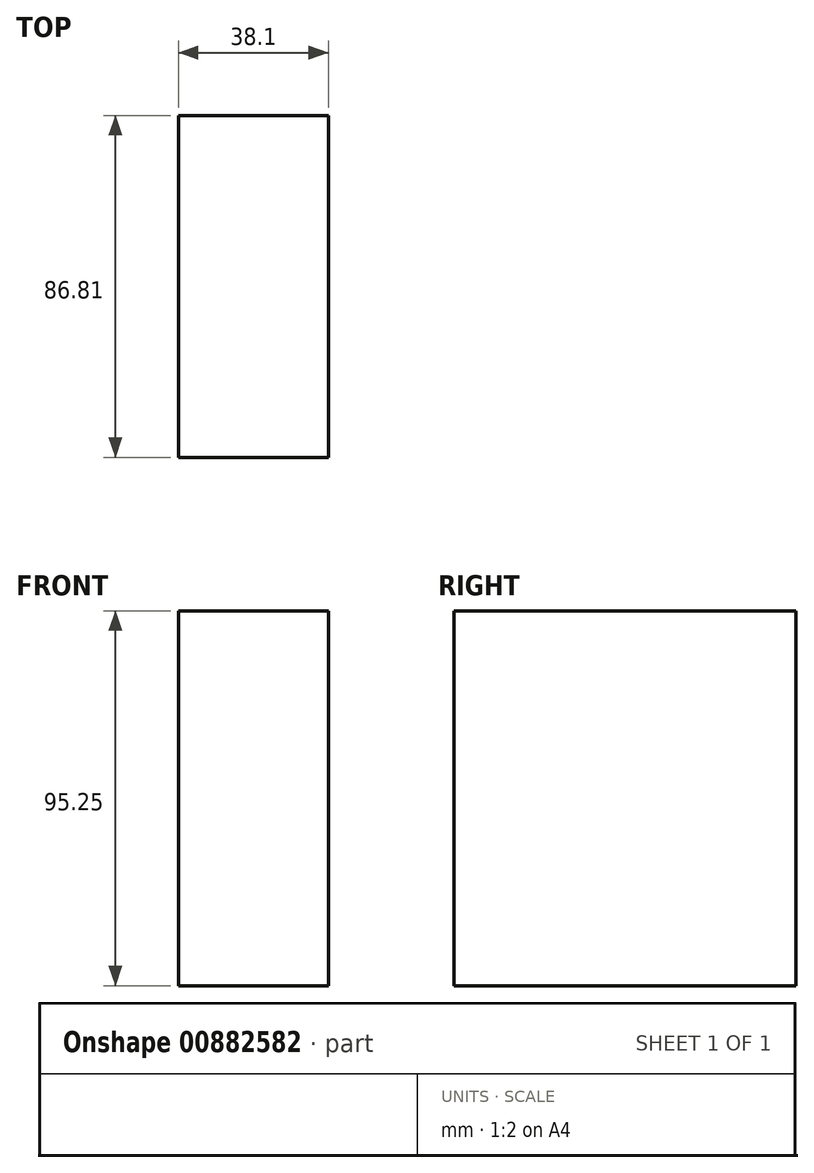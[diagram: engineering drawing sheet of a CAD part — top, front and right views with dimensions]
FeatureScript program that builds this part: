
annotation { "Feature Type Name" : "Feature", "Feature Type Description" : "" }
export const myFeature = defineFeature(function(context is Context, id is Id, definition is map)
    precondition{}
    {
        {
            var Q0;
            Q0=qCreatedBy(makeId("Front.planeOp"),FACE);
            var sketch = newSketch(context, id + "F0", { "sketchPlane" : qUnion([Q0])});
            skLineSegment(sketch, "E0.bottom", {"start": v(0, 0) * mm, "end": v(76.2, 0) * mm});
            skLineSegment(sketch, "E0.top", {"start": v(0, 95.25) * mm, "end": v(76.2, 95.25) * mm});
            skLineSegment(sketch, "E0.left", {"start": v(0, 0) * mm, "end": v(0, 95.25) * mm});
            skLineSegment(sketch, "E0.right", {"start": v(76.2, 0) * mm, "end": v(76.2, 95.25) * mm});
            skSolve(sketch);
        }
        {
            var Q0;
            Q0=makeQuery(id+"F0.imprint","IMPRINT",FACE,{"disambiguationData":[TD([[makeQuery(id+"F0.imprint","IMPRINT",EDGE,{"derivedFrom":sQuery(id+"F0.wireOp",EDGE,"E0.bottom")}),1.0]])]});
            extrude(context, id + "F1", {"entities" : qUnion([Q0]), "depth" : ((94.5 - 2.94) - 4.75) * mm, "offsetDistance" : 25.4 * mm});
        }
        {
            var Q0;
            Q0=makeQuery(id+"F1.opExtrude","SWEPT_FACE",FACE,{"disambiguationData":[OSD([sQuery(id+"F0.wireOp",EDGE,"E0.left")])]});
            var sketch = newSketch(context, id + "F2", { "sketchPlane" : qUnion([Q0])});
            skLineSegment(sketch, "E1.bottom", {"start": v(0, 95.25) * mm, "end": v(95.25, 95.25) * mm});
            skLineSegment(sketch, "E1.top", {"start": v(0, 0) * mm, "end": v(95.25, 0) * mm});
            skLineSegment(sketch, "E1.left", {"start": v(0, 95.25) * mm, "end": v(0, 0) * mm});
            skLineSegment(sketch, "E1.right", {"start": v(95.25, 95.25) * mm, "end": v(95.25, 0) * mm});
            skLineSegment(sketch, "E2.bottom", {"start": v(1528.76, 95.25) * mm, "end": v(1624.01, 95.25) * mm});
            skLineSegment(sketch, "E2.top", {"start": v(1528.76, 0) * mm, "end": v(1624.01, 0) * mm});
            skLineSegment(sketch, "E2.left", {"start": v(1528.76, 95.25) * mm, "end": v(1528.76, 0) * mm});
            skLineSegment(sketch, "E2.right", {"start": v(1624.01, 95.25) * mm, "end": v(1624.01, 0) * mm});
            skLineSegment(sketch, "E3.bottom", {"start": v(2205.04, 0) * mm, "end": v(2109.79, 0) * mm});
            skLineSegment(sketch, "E3.top", {"start": v(2205.04, 95.25) * mm, "end": v(2109.79, 95.25) * mm});
            skLineSegment(sketch, "E3.left", {"start": v(2205.04, 0) * mm, "end": v(2205.04, 95.25) * mm});
            skLineSegment(sketch, "E3.right", {"start": v(2109.79, 0) * mm, "end": v(2109.79, 95.25) * mm});
            skSolve(sketch);
        }
        {
            var Q0;
            Q0 = qSketchRegion(id + "F2", true);
            extrude(context, id + "F3", {"entities" : qUnion([Q0]), "operationType" : NewBodyOperationType.REMOVE, "oppositeDirection" : true, "depth" : 38.1 * mm, "offsetDistance" : 25.4 * mm});
        }
    });
